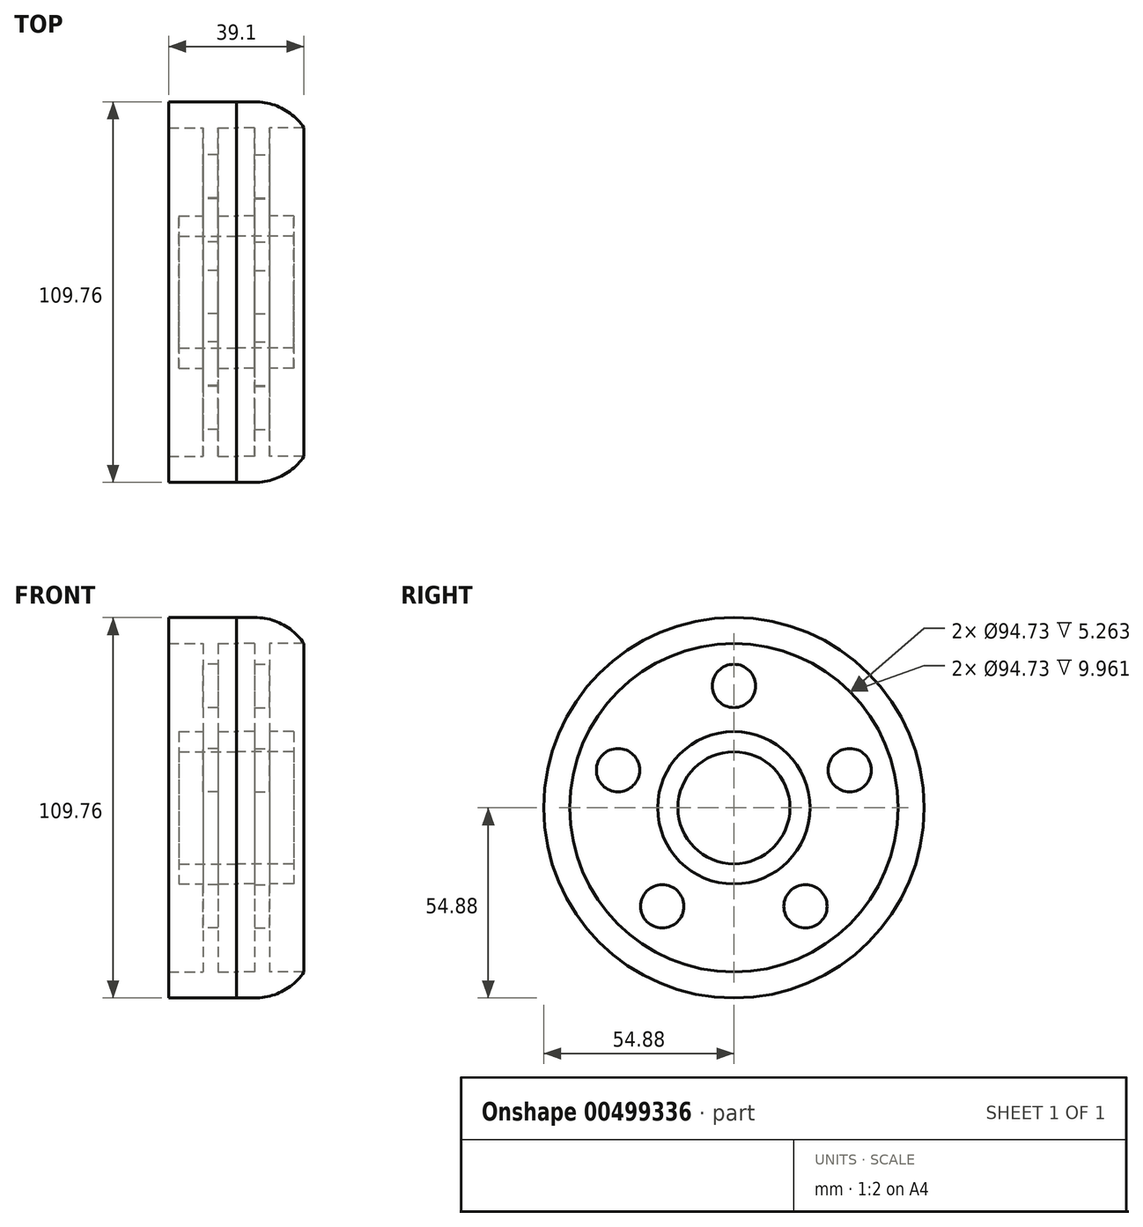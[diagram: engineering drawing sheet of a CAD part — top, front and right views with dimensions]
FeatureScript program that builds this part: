
annotation { "Feature Type Name" : "Feature", "Feature Type Description" : "" }
export const myFeature = defineFeature(function(context is Context, id is Id, definition is map)
    precondition{}
    {
        {
            var Q0;
            Q0=qCreatedBy(makeId("Front.planeOp"),FACE);
            var sketch = newSketch(context, id + "F0", { "sketchPlane" : qUnion([Q0])});
            skLineSegment(sketch, "E0", {"start": v(0, 0) * mm, "end": v(12.78, 0) * mm});
            skLineSegment(sketch, "E1", {"start": v(0, 54.88) * mm, "end": v(19.55, 54.88) * mm});
            skLineSegment(sketch, "E2", {"start": v(19.55, 47.36) * mm, "end": v(19.55, 54.88) * mm});
            skLineSegment(sketch, "E3", {"start": v(9.59, 47.36) * mm, "end": v(19.55, 47.36) * mm});
            skLineSegment(sketch, "E4", {"start": v(9.59, 21.99) * mm, "end": v(9.59, 47.36) * mm});
            skLineSegment(sketch, "E5", {"start": v(9.59, 21.99) * mm, "end": v(16.54, 21.99) * mm});
            skLineSegment(sketch, "E6", {"start": v(16.54, 21.99) * mm, "end": v(16.54, 16.16) * mm});
            skLineSegment(sketch, "E7", {"start": v(16.54, 16.16) * mm, "end": v(0, 16.16) * mm});
            skLineSegment(sketch, "E8", {"start": v(0, 16.16) * mm, "end": v(0, 21.99) * mm});
            skLineSegment(sketch, "E9", {"start": v(0, 21.99) * mm, "end": v(5.26, 21.99) * mm});
            skLineSegment(sketch, "E10", {"start": v(5.26, 21.99) * mm, "end": v(5.26, 47.36) * mm});
            skLineSegment(sketch, "E11", {"start": v(5.26, 47.36) * mm, "end": v(0, 47.36) * mm});
            skLineSegment(sketch, "E12", {"start": v(0, 47.36) * mm, "end": v(0, 54.88) * mm});
            skSolve(sketch);
        }
        {
            var Q0;
            Q0 = qSketchRegion(id + "F0", true);
            var Q1;
            Q1=sQuery(id+"F0.wireOp",EDGE,"E0");
            revolve(context, id + "F1", {"entities" : qUnion([Q0]), "axis" : qUnion([Q1]), "revolveType" : RevolveType.FULL});
        }
        {
            var Q0;
            Q0=makeQuery(id+"F1.opRevolve","SWEPT_FACE",FACE,{"disambiguationData":[OSD([sQuery(id+"F0.wireOp",EDGE,"E4")])]});
            var sketch = newSketch(context, id + "F2", { "sketchPlane" : qUnion([Q0])});
            skCircle(sketch, "E13", {"center": v(0, 35.15) * mm, "radius": 6.25 * mm});
            skCircle(sketch, "E14.1.0", {"center": v(-33.43, 10.86) * mm, "radius": 6.25 * mm});
            skCircle(sketch, "E14.2.0", {"center": v(-20.66, -28.43) * mm, "radius": 6.25 * mm});
            skCircle(sketch, "E14.3.0", {"center": v(20.66, -28.43) * mm, "radius": 6.25 * mm});
            skCircle(sketch, "E14.4.0", {"center": v(33.43, 10.86) * mm, "radius": 6.25 * mm});
            skPoint(sketch, "E14.center", {"position": v(0, 0) * mm});
            skSolve(sketch);
        }
        {
            var Q0;
            Q0=makeQuery(id+"F2.imprint","IMPRINT",FACE,{"disambiguationData":[TD([[makeQuery(id+"F2.imprint","IMPRINT",EDGE,{"derivedFrom":sQuery(id+"F2.wireOp",EDGE,"E13")}),1.0]])]});
            var Q1;
            Q1=makeQuery(id+"F2.imprint","IMPRINT",FACE,{"disambiguationData":[TD([[makeQuery(id+"F2.imprint","IMPRINT",EDGE,{"derivedFrom":sQuery(id+"F2.wireOp",EDGE,"E14.1.0")}),1.0]])]});
            var Q2;
            Q2=makeQuery(id+"F2.imprint","IMPRINT",FACE,{"disambiguationData":[TD([[makeQuery(id+"F2.imprint","IMPRINT",EDGE,{"derivedFrom":sQuery(id+"F2.wireOp",EDGE,"E14.4.0")}),1.0]])]});
            var Q3;
            Q3=makeQuery(id+"F2.imprint","IMPRINT",FACE,{"disambiguationData":[TD([[makeQuery(id+"F2.imprint","IMPRINT",EDGE,{"derivedFrom":sQuery(id+"F2.wireOp",EDGE,"E14.3.0")}),1.0]])]});
            var Q4;
            Q4=makeQuery(id+"F2.imprint","IMPRINT",FACE,{"disambiguationData":[TD([[makeQuery(id+"F2.imprint","IMPRINT",EDGE,{"derivedFrom":sQuery(id+"F2.wireOp",EDGE,"E14.2.0")}),1.0]])]});
            extrude(context, id + "F3", {"entities" : qUnion([Q0, Q1, Q2, Q3, Q4]), "operationType" : NewBodyOperationType.REMOVE, "oppositeDirection" : true, "depth" : 25 * mm});
        }
        {
            var Q0;
            Q0=makeQuery(id+"F1.opRevolve","SWEPT_BODY",BODY,{"disambiguationData":[OSD([sQuery(id+"F0.wireOp",EDGE,"E1"),sQuery(id+"F0.wireOp",EDGE,"E2"),sQuery(id+"F0.wireOp",EDGE,"E3"),sQuery(id+"F0.wireOp",EDGE,"E4"),sQuery(id+"F0.wireOp",EDGE,"E5"),sQuery(id+"F0.wireOp",EDGE,"E6"),sQuery(id+"F0.wireOp",EDGE,"E7"),sQuery(id+"F0.wireOp",EDGE,"E8"),sQuery(id+"F0.wireOp",EDGE,"E9"),sQuery(id+"F0.wireOp",EDGE,"E10"),sQuery(id+"F0.wireOp",EDGE,"E11"),sQuery(id+"F0.wireOp",EDGE,"E12")])]});
            var Q1;
            Q1=qCreatedBy(makeId("Right.planeOp"),FACE);
            mirror(context, id + "F4", {"entities" : qUnion([Q0]), "mirrorPlane" : qUnion([Q1])});
        }
        {
            var Q0;
            Q0=makeQuery(id+"F1.opRevolve","SWEPT_EDGE",EDGE,{"disambiguationData":[OSD([sQuery(id+"F0.wireOp",EDGE,"E1"),sQuery(id+"F0.wireOp",EDGE,"E2")])]});
            fillet(context, id + "F5", {"entities" : qUnion([Q0]), "radius" : 17.17 * mm, "tangentPropagation" : true, "allowEdgeOverflow" : false});
        }
    });
